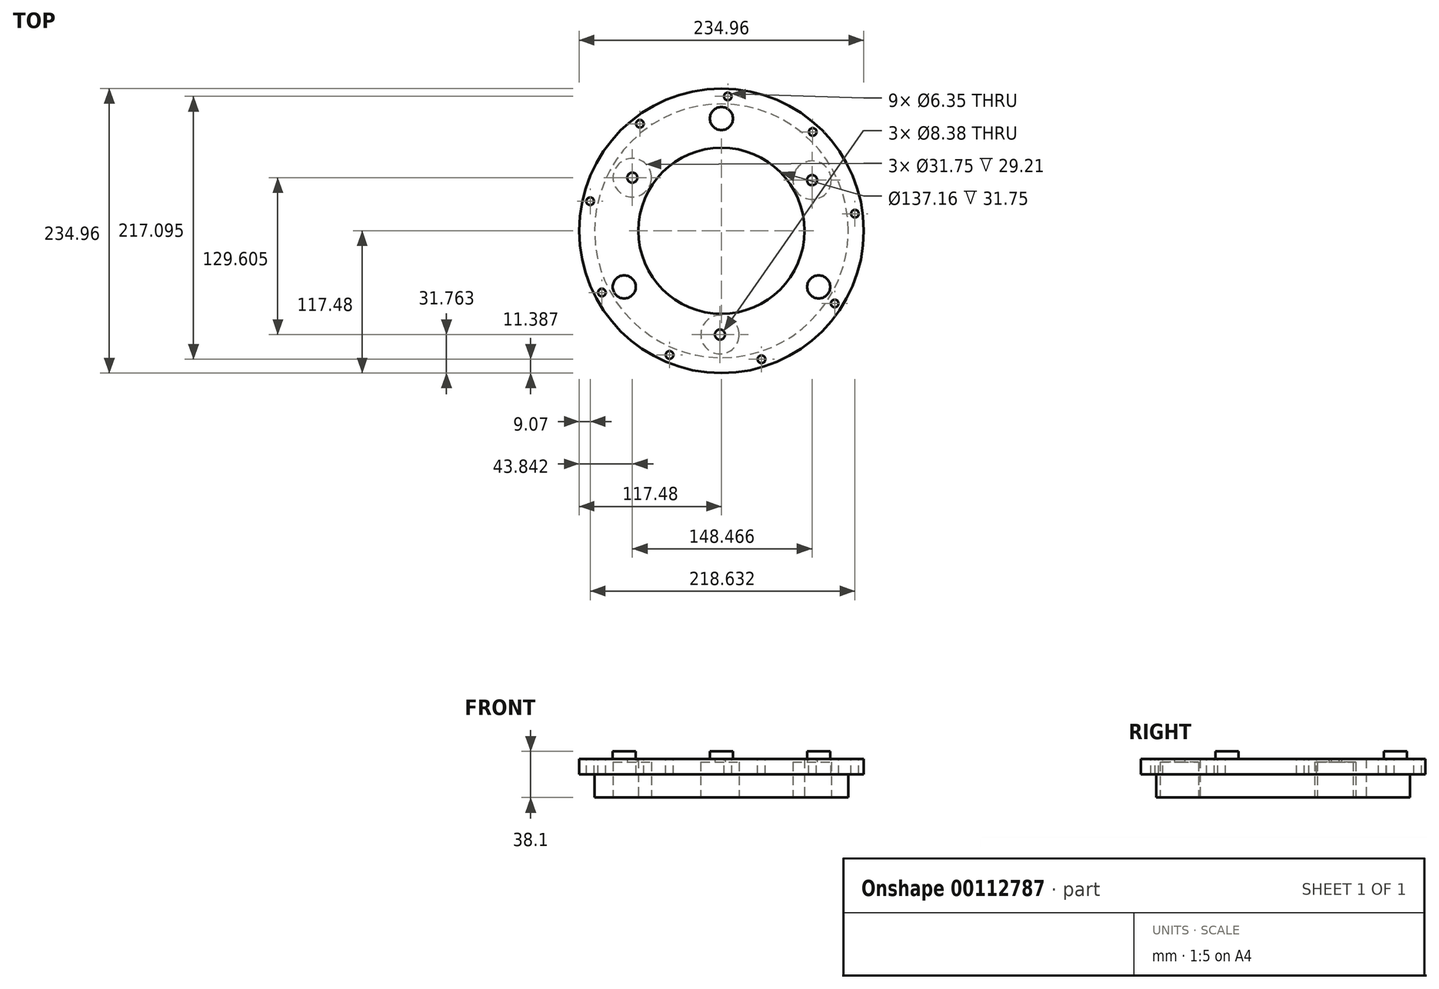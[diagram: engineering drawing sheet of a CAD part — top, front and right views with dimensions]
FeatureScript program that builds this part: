
annotation { "Feature Type Name" : "Feature", "Feature Type Description" : "" }
export const myFeature = defineFeature(function(context is Context, id is Id, definition is map)
    precondition{}
    {
        {
            var Q0;
            Q0=qCreatedBy(makeId("Top.planeOp"),FACE);
            var sketch = newSketch(context, id + "F0", { "sketchPlane" : qUnion([Q0])});
            skCircle(sketch, "E0", {"center": v(0, 0) * mm, "radius": 117.47 * mm});
            skSolve(sketch);
        }
        {
            var Q0;
            Q0=makeQuery(id+"F0.imprint","IMPRINT",FACE,{"disambiguationData":[TD([[makeQuery(id+"F0.imprint","IMPRINT",EDGE,{"derivedFrom":sQuery(id+"F0.wireOp",EDGE,"E0")}),1.0]])]});
            extrude(context, id + "F1", {"entities" : qUnion([Q0]), "depth" : 12.7 * mm});
        }
        {
            var Q0;
            Q0=makeQuery(id+"F1.opExtrude","CAP_FACE",FACE,{"disambiguationData":[OSD([sQuery(id+"F0.wireOp",EDGE,"E0")])],"isStart":true});
            var sketch = newSketch(context, id + "F2", { "sketchPlane" : qUnion([Q0])});
            skCircle(sketch, "E1", {"center": v(0, 0) * mm, "radius": 104.78 * mm});
            skSolve(sketch);
        }
        {
            var Q0;
            Q0 = qSketchRegion(id + "F2", true);
            extrude(context, id + "F3", {"entities" : qUnion([Q0]), "operationType" : NewBodyOperationType.ADD, "depth" : 19.05 * mm});
        }
        {
            var Q0;
            Q0=makeQuery(id+"F1.opExtrude","CAP_FACE",FACE,{"disambiguationData":[OSD([sQuery(id+"F0.wireOp",EDGE,"E0")])],"isStart":false});
            var sketch = newSketch(context, id + "F4", { "sketchPlane" : qUnion([Q0])});
            skSolve(sketch);
        }
        {
            var Q0;
            Q0=makeQuery(id+"F4.imprint","IMPRINT",FACE,{"disambiguationData":[TD([[makeQuery(id+"F4.imprint","IMPRINT",EDGE,{"derivedFrom":makeQuery(id+"F1.opExtrude","CAP_EDGE",EDGE,{"disambiguationData":[OSD([sQuery(id+"F0.wireOp",EDGE,"E0")])],"isStart":false})}),1.0]])]});
            var sketch = newSketch(context, id + "F5", { "sketchPlane" : qUnion([Q0])});
            skPoint(sketch, "E2.center", {"position": v(0, 0) * mm});
            skCircle(sketch, "E3", {"center": v(-42.87, -102.52) * mm, "radius": 1.59 * mm});
            skCircle(sketch, "E4.1.0", {"center": v(33.06, -106.1) * mm, "radius": 1.59 * mm});
            skCircle(sketch, "E4.2.0", {"center": v(93.52, -60.02) * mm, "radius": 1.59 * mm});
            skCircle(sketch, "E4.3.0", {"center": v(110.22, 14.14) * mm, "radius": 1.59 * mm});
            skCircle(sketch, "E4.4.0", {"center": v(75.35, 81.68) * mm, "radius": 1.59 * mm});
            skCircle(sketch, "E4.5.0", {"center": v(5.22, 111) * mm, "radius": 1.59 * mm});
            skCircle(sketch, "E4.6.0", {"center": v(-67.35, 88.39) * mm, "radius": 1.59 * mm});
            skCircle(sketch, "E4.7.0", {"center": v(-108.4, 24.41) * mm, "radius": 1.59 * mm});
            skCircle(sketch, "E4.8.0", {"center": v(-98.74, -50.98) * mm, "radius": 1.59 * mm});
            skSolve(sketch);
        }
        {
            var Q0;
            Q0=sQuery(id+"F5.wireOp",VERTEX,"E4.7.0.center");
            var Q1;
            Q1=sQuery(id+"F5.wireOp",VERTEX,"E4.8.0.center");
            var Q2;
            Q2=sQuery(id+"F5.wireOp",VERTEX,"E3.center");
            var Q3;
            Q3=sQuery(id+"F5.wireOp",VERTEX,"E4.1.0.center");
            var Q4;
            Q4=sQuery(id+"F5.wireOp",VERTEX,"E4.2.0.center");
            var Q5;
            Q5=sQuery(id+"F5.wireOp",VERTEX,"E4.3.0.center");
            var Q6;
            Q6=sQuery(id+"F5.wireOp",VERTEX,"E4.4.0.center");
            var Q7;
            Q7=sQuery(id+"F5.wireOp",VERTEX,"E4.6.0.center");
            var Q8;
            Q8=sQuery(id+"F5.wireOp",VERTEX,"E4.5.0.center");
            var Q9;
            Q9=makeQuery(id+"F1.opExtrude","SWEPT_BODY",BODY,{"disambiguationData":[OSD([sQuery(id+"F0.wireOp",EDGE,"E0")])]});
            hole(context, id + "F6", {"style" : HoleStyle.SIMPLE, "endStyle" : HoleEndStyle.THROUGH, "holeDiameter" : 6.35 * mm, "locations" : qUnion([Q0, Q1, Q2, Q3, Q4, Q5, Q6, Q7, Q8]), "scope" : qUnion([Q9]), "isTappedThrough" : true});
        }
        {
            var Q0;
            Q0=makeQuery(id+"F3.opExtrude","CAP_FACE",FACE,{"disambiguationData":[OSD([sQuery(id+"F2.wireOp",EDGE,"E1")])],"isStart":false});
            var sketch = newSketch(context, id + "F7", { "sketchPlane" : qUnion([Q0])});
            skCircle(sketch, "E5", {"center": v(74.83, -41.83) * mm, "radius": 3.81 * mm});
            skCircle(sketch, "E6.1.0", {"center": v(-1.19, 85.72) * mm, "radius": 3.81 * mm});
            skCircle(sketch, "E6.2.0", {"center": v(-73.64, -43.89) * mm, "radius": 3.81 * mm});
            skPoint(sketch, "E6.center", {"position": v(0, 0) * mm});
            skSolve(sketch);
        }
        {
            var Q0;
            Q0=sQuery(id+"F7.wireOp",VERTEX,"E5.center");
            var Q1;
            Q1=sQuery(id+"F7.wireOp",VERTEX,"E6.2.0.center");
            var Q2;
            Q2=sQuery(id+"F7.wireOp",VERTEX,"E6.1.0.center");
            var Q3;
            Q3=makeQuery(id+"F1.opExtrude","SWEPT_BODY",BODY,{"disambiguationData":[OSD([sQuery(id+"F0.wireOp",EDGE,"E0")])]});
            hole(context, id + "F8", {"style" : HoleStyle.SIMPLE, "endStyle" : HoleEndStyle.THROUGH, "holeDiameter" : 8.38 * mm, "locations" : qUnion([Q0, Q1, Q2]), "scope" : qUnion([Q3]), "isTappedThrough" : true});
        }
        {
            var Q0;
            Q0=makeQuery(id+"F3.opExtrude","CAP_FACE",FACE,{"disambiguationData":[OSD([sQuery(id+"F2.wireOp",EDGE,"E1")])],"isStart":false});
            var sketch = newSketch(context, id + "F9", { "sketchPlane" : qUnion([Q0])});
            skCircle(sketch, "E7", {"center": v(74.83, -41.83) * mm, "radius": 15.88 * mm});
            skCircle(sketch, "E8.1.0", {"center": v(-1.19, 85.72) * mm, "radius": 15.88 * mm});
            skCircle(sketch, "E8.2.0", {"center": v(-73.64, -43.89) * mm, "radius": 15.88 * mm});
            skPoint(sketch, "E8.center", {"position": v(0, 0) * mm});
            skSolve(sketch);
        }
        {
            var Q0;
            Q0=makeQuery(id+"F9.imprint","IMPRINT",FACE,{"disambiguationData":[TD([[makeQuery(id+"F9.imprint","IMPRINT",EDGE,{"derivedFrom":sQuery(id+"F9.wireOp",EDGE,"E8.2.0")}),1.0]])]});
            var Q1;
            Q1=makeQuery(id+"F9.imprint","IMPRINT",FACE,{"disambiguationData":[TD([[makeQuery(id+"F9.imprint","IMPRINT",EDGE,{"derivedFrom":sQuery(id+"F9.wireOp",EDGE,"E8.1.0")}),1.0]])]});
            var Q2;
            Q2=makeQuery(id+"F9.imprint","IMPRINT",FACE,{"disambiguationData":[TD([[makeQuery(id+"F9.imprint","IMPRINT",EDGE,{"derivedFrom":sQuery(id+"F9.wireOp",EDGE,"E7")}),1.0]])]});
            extrude(context, id + "F10", {"entities" : qUnion([Q0, Q1, Q2]), "operationType" : NewBodyOperationType.REMOVE, "oppositeDirection" : true, "depth" : 29.2 * mm});
        }
        {
            var Q0;
            Q0=makeQuery(id+"F3.opExtrude","CAP_FACE",FACE,{"disambiguationData":[OSD([sQuery(id+"F2.wireOp",EDGE,"E1")])],"isStart":false});
            var sketch = newSketch(context, id + "F11", { "sketchPlane" : qUnion([Q0])});
            skCircle(sketch, "E9", {"center": v(0, 0) * mm, "radius": 68.58 * mm});
            skSolve(sketch);
        }
        {
            var Q0;
            Q0 = qSketchRegion(id + "F11", true);
            extrude(context, id + "F12", {"entities" : qUnion([Q0]), "operationType" : NewBodyOperationType.REMOVE, "endBound" : BoundingType.THROUGH_ALL, "oppositeDirection" : true, "depth" : 25.4 * mm});
        }
        {
            var Q0;
            Q0=makeQuery(id+"F1.opExtrude","CAP_FACE",FACE,{"disambiguationData":[OSD([sQuery(id+"F0.wireOp",EDGE,"E0")])],"isStart":false});
            var sketch = newSketch(context, id + "F13", { "sketchPlane" : qUnion([Q0])});
            skCircle(sketch, "E10", {"center": v(0, 92.7) * mm, "radius": 9.53 * mm});
            skCircle(sketch, "E11.1.0", {"center": v(-80.29, -46.35) * mm, "radius": 9.53 * mm});
            skCircle(sketch, "E11.2.0", {"center": v(80.29, -46.35) * mm, "radius": 9.53 * mm});
            skPoint(sketch, "E11.center", {"position": v(0, 0) * mm});
            skSolve(sketch);
        }
        {
            var Q0;
            Q0=makeQuery(id+"F13.imprint","IMPRINT",FACE,{"disambiguationData":[TD([[makeQuery(id+"F13.imprint","IMPRINT",EDGE,{"derivedFrom":sQuery(id+"F13.wireOp",EDGE,"E10")}),1.0]])]});
            var Q1;
            Q1=makeQuery(id+"F13.imprint","IMPRINT",FACE,{"disambiguationData":[TD([[makeQuery(id+"F13.imprint","IMPRINT",EDGE,{"derivedFrom":sQuery(id+"F13.wireOp",EDGE,"E11.2.0")}),1.0]])]});
            var Q2;
            Q2=makeQuery(id+"F13.imprint","IMPRINT",FACE,{"disambiguationData":[TD([[makeQuery(id+"F13.imprint","IMPRINT",EDGE,{"derivedFrom":sQuery(id+"F13.wireOp",EDGE,"E11.1.0")}),1.0]])]});
            extrude(context, id + "F14", {"entities" : qUnion([Q0, Q1, Q2]), "operationType" : NewBodyOperationType.ADD, "depth" : 6.35 * mm});
        }
    });
